# Revit family: Shower_Head-Grohe-Rainshower-26570000_Series
name_source: partatom
category: Plumbing Fixtures
revit_build: Autodesk Revit 2018 (Build: 20170223_1515(x64)
units: mm (PartAtom-declared; Revit-internal decimal feet)

## family parameters
Always vertical = No
Cut with Voids When Loaded = No
OmniClass Number = 23.45.05.14.17
OmniClass Title = Showers
Part Type = Normal
Room Calculation Point = No
Round Connector Dimension = Use Diameter
Shared = Yes
Work Plane-Based = Yes

## types (2) — shared parameters
Assembly Code = D2010710
CW Connection = No
CWFU = 3
CalGreen Compliant = Yes
Default Elevation = 74"
Description = Rainshower™ 310 Mono Shower Head, 12in - 1 Spray, 1.75 gpm
Flow Rate = 1.75 gpm (6.6 l/min) flow limiter
HW Connection = No
HWFU = 3
Height = 1/2"
Installation Type = Pipe/Ceiling Mounted
Length = 12 3/16"
Manufacturer = Grohe
Product Documentation Link = https://americanstandard.box.com
Product Page URL = https://www.grohe.us
Tempered Water Connection = Yes
Tempered Water Connection Diameter = 1/2"
URL = https://www.grohe.us
Vent Connection = No
Waste Connection = No
Width = 12 3/16"
cUPC Compliant = Yes
zero-valued in all types: WFU

## per-type parameters (varying)
| type | Compliance Certifications | Finish | Material |
| 26570000 | Energy Policy Act of 1992, ASME A112.18.1/CSA B125.1 | Plastic-Grohe-000-StarLight Chrome | Plastic-Grohe-000-StarLight Chrome |
| 26570EN0 | Energy Policy Act of 1992, ASME A112.18.1/CSA B125.1, EPA WaterSense | Plasstic-Grohe-EN0-Brushed Nickel Infinity Finish | Plasstic-Grohe-EN0-Brushed Nickel Infinity Finish |

note: column(s) folded — value = type name in every type: Model

## geometry (parser evidence)
native form markers: Sweep x2
no freeform markers — native parametric forms only
